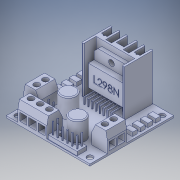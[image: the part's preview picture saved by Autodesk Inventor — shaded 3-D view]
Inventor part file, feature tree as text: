
AUTODESK INVENTOR PART (.ipt)
format: ipt  version: 2016 (Build 200138000, 138)  size: 696,320 bytes
history: native  units: in
note: dims shown in document units (in); Inventor stores cm internally (conversion verified against a paired STEP export)
features: fillet x1
ambient origin geometry x8: Origin, YZ Plane, XZ Plane, XY Plane, X Axis, Y Axis, Z Axis, Center Point
bodies: Solid1 (feature_tree)
feature tree (1):
  fillet  "Redondeo2"  [1 undecoded]
note: 1 required parameter value undecoded (feature->parameter linkage not recoverable at this tier; creation-order binding heuristic only, values carry confidence <= 0.55)
